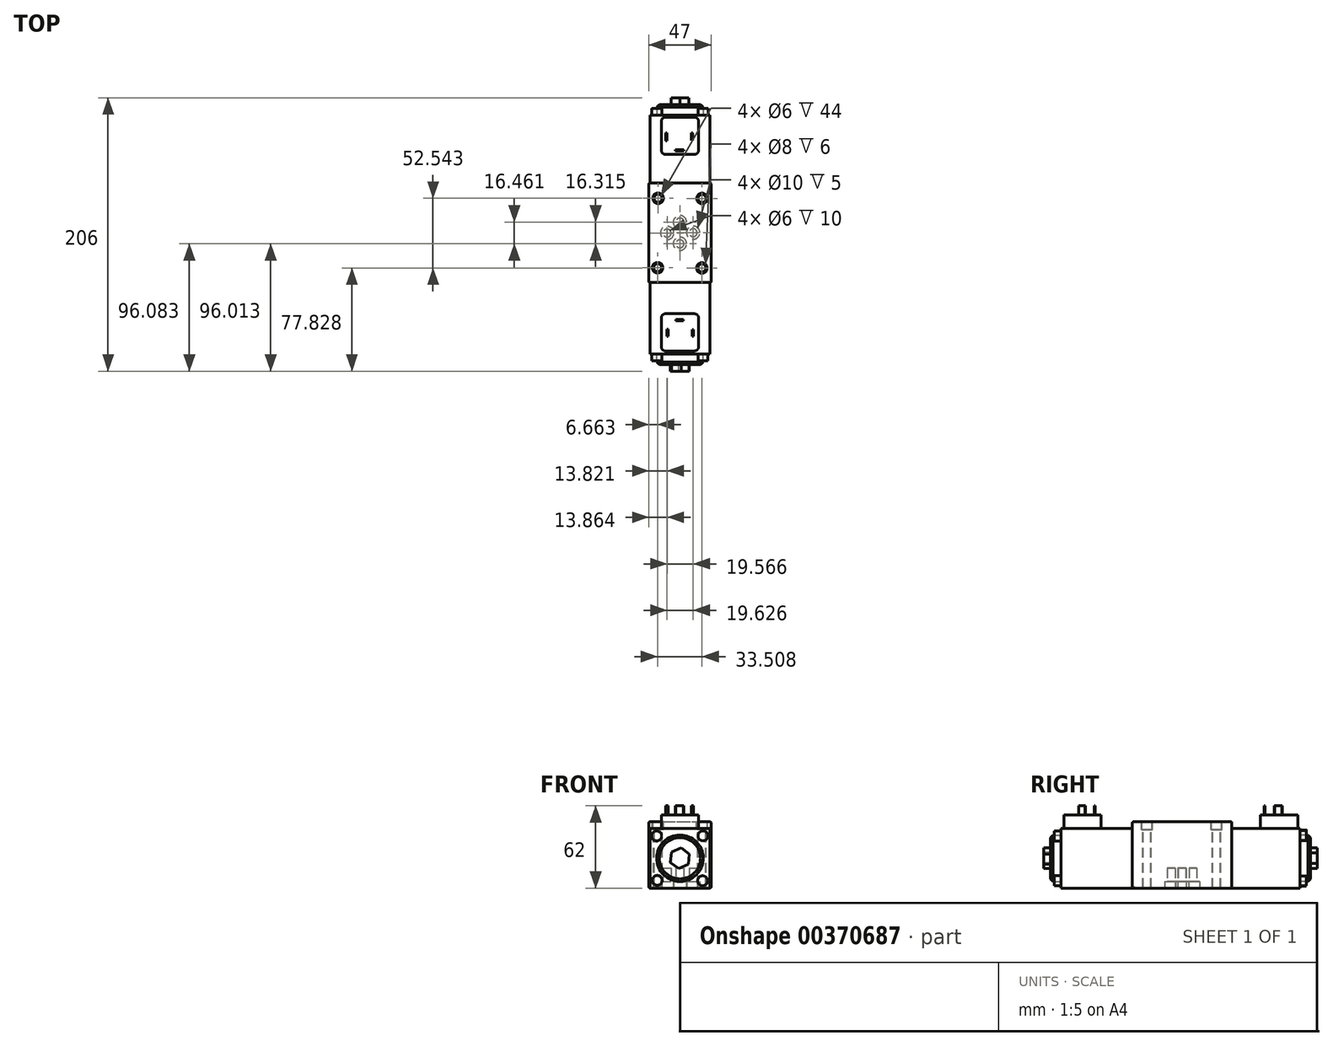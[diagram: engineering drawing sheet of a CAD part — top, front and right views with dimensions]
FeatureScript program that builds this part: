
annotation { "Feature Type Name" : "Feature", "Feature Type Description" : "" }
export const myFeature = defineFeature(function(context is Context, id is Id, definition is map)
    precondition{}
    {
        {
            var Q0;
            Q0=qCreatedBy(makeId("Front.planeOp"),FACE);
            var sketch = newSketch(context, id + "F0", { "sketchPlane" : qUnion([Q0])});
            skLineSegment(sketch, "E0.bottom", {"start": v(-22.5, 22.5) * mm, "end": v(22.5, 22.5) * mm});
            skLineSegment(sketch, "E0.top", {"start": v(-22.5, -22.5) * mm, "end": v(22.5, -22.5) * mm});
            skLineSegment(sketch, "E0.left", {"start": v(-22.5, 22.5) * mm, "end": v(-22.5, -22.5) * mm});
            skLineSegment(sketch, "E0.right", {"start": v(22.5, 22.5) * mm, "end": v(22.5, -22.5) * mm});
            skPoint(sketch, "E0.middle", {"position": v(0, 0) * mm});
            skSolve(sketch);
        }
        {
            var Q0;
            Q0=makeQuery(id+"F0.imprint","IMPRINT",FACE,{"disambiguationData":[TD([[makeQuery(id+"F0.imprint","IMPRINT",EDGE,{"derivedFrom":sQuery(id+"F0.wireOp",EDGE,"E0.bottom")}),-1.0]])]});
            extrude(context, id + "F1", {"entities" : qUnion([Q0]), "oppositeDirection" : true, "depth" : 180 * mm});
        }
        {
            var Q0;
            Q0=makeQuery(id+"F1.opExtrude","CAP_FACE",FACE,{"disambiguationData":[OSD([sQuery(id+"F0.wireOp",EDGE,"E0.bottom"),sQuery(id+"F0.wireOp",EDGE,"E0.top"),sQuery(id+"F0.wireOp",EDGE,"E0.left"),sQuery(id+"F0.wireOp",EDGE,"E0.right")])],"isStart":true});
            var sketch = newSketch(context, id + "F2", { "sketchPlane" : qUnion([Q0])});
            skCircle(sketch, "E1", {"center": v(0, 0) * mm, "radius": 17.5 * mm});
            skSolve(sketch);
        }
        {
            var Q0;
            Q0=makeQuery(id+"F2.imprint","IMPRINT",FACE,{"disambiguationData":[TD([[makeQuery(id+"F2.imprint","IMPRINT",EDGE,{"derivedFrom":sQuery(id+"F2.wireOp",EDGE,"E1")}),1.0]])]});
            extrude(context, id + "F3", {"entities" : qUnion([Q0]), "operationType" : NewBodyOperationType.ADD, "depth" : 8 * mm});
        }
        {
            var Q0;
            Q0=makeQuery(id+"F1.opExtrude","CAP_FACE",FACE,{"disambiguationData":[OSD([sQuery(id+"F0.wireOp",EDGE,"E0.bottom"),sQuery(id+"F0.wireOp",EDGE,"E0.top"),sQuery(id+"F0.wireOp",EDGE,"E0.left"),sQuery(id+"F0.wireOp",EDGE,"E0.right")])],"isStart":false});
            var sketch = newSketch(context, id + "F4", { "sketchPlane" : qUnion([Q0])});
            skCircle(sketch, "E2", {"center": v(0, 0) * mm, "radius": 17.5 * mm});
            skSolve(sketch);
        }
        {
            var Q0;
            Q0=makeQuery(id+"F4.imprint","IMPRINT",FACE,{"disambiguationData":[TD([[makeQuery(id+"F4.imprint","IMPRINT",EDGE,{"derivedFrom":sQuery(id+"F4.wireOp",EDGE,"E2")}),1.0]])]});
            extrude(context, id + "F5", {"entities" : qUnion([Q0]), "operationType" : NewBodyOperationType.ADD, "depth" : 8 * mm});
        }
        {
            var Q0;
            Q0=makeQuery(id+"F1.opExtrude","CAP_FACE",FACE,{"disambiguationData":[OSD([sQuery(id+"F0.wireOp",EDGE,"E0.bottom"),sQuery(id+"F0.wireOp",EDGE,"E0.top"),sQuery(id+"F0.wireOp",EDGE,"E0.left"),sQuery(id+"F0.wireOp",EDGE,"E0.right")])],"isStart":false});
            var sketch = newSketch(context, id + "F6", { "sketchPlane" : qUnion([Q0])});
            skSolve(sketch);
        }
        {
            var Q0;
            Q0=makeQuery(id+"F1.opExtrude","CAP_FACE",FACE,{"disambiguationData":[OSD([sQuery(id+"F0.wireOp",EDGE,"E0.bottom"),sQuery(id+"F0.wireOp",EDGE,"E0.top"),sQuery(id+"F0.wireOp",EDGE,"E0.left"),sQuery(id+"F0.wireOp",EDGE,"E0.right")])],"isStart":true});
            var sketch = newSketch(context, id + "F7", { "sketchPlane" : qUnion([Q0])});
            skCircle(sketch, "E3", {"center": v(17.33, 16.83) * mm, "radius": 3.75 * mm});
            skCircle(sketch, "E4", {"center": v(-17.5, 16.75) * mm, "radius": 3.75 * mm});
            skCircle(sketch, "E5", {"center": v(-17.1, -16.62) * mm, "radius": 3.75 * mm});
            skCircle(sketch, "E6", {"center": v(17.1, -16.96) * mm, "radius": 3.75 * mm});
            skSolve(sketch);
        }
        {
            var Q0;
            Q0=makeQuery(id+"F7.imprint","IMPRINT",FACE,{"disambiguationData":[TD([[makeQuery(id+"F7.imprint","IMPRINT",EDGE,{"derivedFrom":sQuery(id+"F7.wireOp",EDGE,"E6")}),1.0]])]});
            var Q1;
            Q1=makeQuery(id+"F7.imprint","IMPRINT",FACE,{"disambiguationData":[TD([[makeQuery(id+"F7.imprint","IMPRINT",EDGE,{"derivedFrom":sQuery(id+"F7.wireOp",EDGE,"E5")}),1.0]])]});
            var Q2;
            Q2=makeQuery(id+"F7.imprint","IMPRINT",FACE,{"disambiguationData":[TD([[makeQuery(id+"F7.imprint","IMPRINT",EDGE,{"derivedFrom":sQuery(id+"F7.wireOp",EDGE,"E3")}),1.0]])]});
            var Q3;
            Q3=makeQuery(id+"F7.imprint","IMPRINT",FACE,{"disambiguationData":[TD([[makeQuery(id+"F7.imprint","IMPRINT",EDGE,{"derivedFrom":sQuery(id+"F7.wireOp",EDGE,"E4")}),1.0]])]});
            extrude(context, id + "F8", {"entities" : qUnion([Q0, Q1, Q2, Q3]), "operationType" : NewBodyOperationType.ADD, "depth" : 5 * mm});
        }
        {
            var Q0;
            Q0=makeQuery(id+"F3.opExtrude","CAP_FACE",FACE,{"disambiguationData":[OSD([sQuery(id+"F2.wireOp",EDGE,"E1")])],"isStart":false});
            var sketch = newSketch(context, id + "F9", { "sketchPlane" : qUnion([Q0])});
            skCircle(sketch, "E7.cCircle", {"center": v(0, 0) * mm, "radius": 6.75 * mm, "construction": true});
            skLineSegment(sketch, "E7.0", {"start": v(-6.28, 4.61) * mm, "end": v(0.85, 7.75) * mm});
            skLineSegment(sketch, "E7.1", {"start": v(0.85, 7.75) * mm, "end": v(7.14, 3.13) * mm});
            skLineSegment(sketch, "E7.2", {"start": v(7.14, 3.13) * mm, "end": v(6.28, -4.61) * mm});
            skLineSegment(sketch, "E7.3", {"start": v(6.28, -4.61) * mm, "end": v(-0.85, -7.75) * mm});
            skLineSegment(sketch, "E7.4", {"start": v(-0.85, -7.75) * mm, "end": v(-7.14, -3.13) * mm});
            skLineSegment(sketch, "E7.5", {"start": v(-7.14, -3.13) * mm, "end": v(-6.28, 4.61) * mm});
            skPoint(sketch, "E7.0.midPoint", {"position": v(-2.71, 6.18) * mm});
            skSolve(sketch);
        }
        {
            var Q0;
            Q0 = qSketchRegion(id + "F9", true);
            extrude(context, id + "F10", {"entities" : qUnion([Q0]), "operationType" : NewBodyOperationType.ADD, "depth" : 5 * mm});
        }
        {
            var Q0;
            Q0=makeQuery(id+"F5.opExtrude","CAP_FACE",FACE,{"disambiguationData":[OSD([sQuery(id+"F4.wireOp",EDGE,"E2")])],"isStart":false});
            var sketch = newSketch(context, id + "F11", { "sketchPlane" : qUnion([Q0])});
            skCircle(sketch, "E8.cCircle", {"center": v(0, 0) * mm, "radius": 6.75 * mm, "construction": true});
            skLineSegment(sketch, "E8.0", {"start": v(-6.75, -3.9) * mm, "end": v(-6.75, 3.9) * mm});
            skLineSegment(sketch, "E8.1", {"start": v(-6.75, 3.9) * mm, "end": v(0, 7.8) * mm});
            skLineSegment(sketch, "E8.2", {"start": v(0, 7.8) * mm, "end": v(6.75, 3.9) * mm});
            skLineSegment(sketch, "E8.3", {"start": v(6.75, 3.9) * mm, "end": v(6.75, -3.9) * mm});
            skLineSegment(sketch, "E8.4", {"start": v(6.75, -3.9) * mm, "end": v(0, -7.8) * mm});
            skLineSegment(sketch, "E8.5", {"start": v(0, -7.8) * mm, "end": v(-6.75, -3.9) * mm});
            skPoint(sketch, "E8.0.midPoint", {"position": v(-6.75, 0) * mm});
            skSolve(sketch);
        }
        {
            var Q0;
            Q0 = qSketchRegion(id + "F11", true);
            extrude(context, id + "F12", {"entities" : qUnion([Q0]), "operationType" : NewBodyOperationType.ADD, "depth" : 5 * mm});
        }
        {
            var Q0;
            Q0=makeQuery(id+"F6.imprint","IMPRINT",FACE,{"disambiguationData":[TD([[makeQuery(id+"F6.imprint","IMPRINT",EDGE,{"derivedFrom":makeQuery(id+"F1.opExtrude","CAP_EDGE",EDGE,{"disambiguationData":[OSD([sQuery(id+"F0.wireOp",EDGE,"E0.bottom")])],"isStart":false})}),1.0]])]});
            var sketch = newSketch(context, id + "F13", { "sketchPlane" : qUnion([Q0])});
            skCircle(sketch, "E9", {"center": v(-17.56, 17.13) * mm, "radius": 3.75 * mm});
            skCircle(sketch, "E10", {"center": v(17.36, 17.52) * mm, "radius": 3.75 * mm});
            skCircle(sketch, "E11", {"center": v(-17.32, -17.12) * mm, "radius": 3.75 * mm});
            skCircle(sketch, "E12", {"center": v(17.37, -17.42) * mm, "radius": 3.75 * mm});
            skSolve(sketch);
        }
        {
            var Q0;
            Q0 = qSketchRegion(id + "F13", true);
            extrude(context, id + "F14", {"entities" : qUnion([Q0]), "operationType" : NewBodyOperationType.ADD, "depth" : 5 * mm});
        }
        {
            var Q0;
            Q0=makeQuery(id+"F3.opExtrude","CAP_EDGE",EDGE,{"disambiguationData":[OSD([sQuery(id+"F2.wireOp",EDGE,"E1")])],"isStart":false});
            chamfer(context, id + "F15", {"entities" : qUnion([Q0]), "width" : 2 * mm, "tangentPropagation" : true});
        }
        {
            var Q0;
            Q0=makeQuery(id+"F5.opExtrude","CAP_EDGE",EDGE,{"disambiguationData":[OSD([sQuery(id+"F4.wireOp",EDGE,"E2")])],"isStart":false});
            chamfer(context, id + "F16", {"entities" : qUnion([Q0]), "width" : 2 * mm, "tangentPropagation" : true});
        }
        {
            var Q0;
            Q0=makeQuery(id+"F1.opExtrude","SWEPT_FACE",FACE,{"disambiguationData":[OSD([sQuery(id+"F0.wireOp",EDGE,"E0.bottom")])]});
            var sketch = newSketch(context, id + "F17", { "sketchPlane" : qUnion([Q0])});
            skLineSegment(sketch, "E13.bottom", {"start": v(-11, 30.3) * mm, "end": v(11, 30.3) * mm});
            skLineSegment(sketch, "E13.top", {"start": v(-11, 2.3) * mm, "end": v(11, 2.3) * mm});
            skLineSegment(sketch, "E13.left", {"start": v(-14, 27.3) * mm, "end": v(-14, 5.3) * mm});
            skLineSegment(sketch, "E13.right", {"start": v(14, 27.3) * mm, "end": v(14, 5.3) * mm});
            skPoint(sketch, "E13.middle", {"position": v(0, 16.3) * mm});
            skLineSegment(sketch, "E14.bottom", {"start": v(11, 150.42) * mm, "end": v(-11, 150.42) * mm});
            skLineSegment(sketch, "E14.top", {"start": v(11, 178.42) * mm, "end": v(-11, 178.42) * mm});
            skLineSegment(sketch, "E14.left", {"start": v(14, 153.42) * mm, "end": v(14, 175.42) * mm});
            skLineSegment(sketch, "E14.right", {"start": v(-14, 153.42) * mm, "end": v(-14, 175.42) * mm});
            skPoint(sketch, "E14.middle", {"position": v(0, 164.42) * mm});
            skPoint(sketch, "E15.visualSharp", {"position": v(14, 178.42) * mm});
            skArc(sketch, "E15.filletArc", {"start": v(14, 175.42) * mm, "mid": v(13.12, 177.54) * mm, "end": v(11, 178.42) * mm});
            skPoint(sketch, "E16.visualSharp", {"position": v(14, 150.42) * mm});
            skArc(sketch, "E16.filletArc", {"start": v(11, 150.42) * mm, "mid": v(13.12, 151.3) * mm, "end": v(14, 153.42) * mm});
            skPoint(sketch, "E17.visualSharp", {"position": v(-14, 150.42) * mm});
            skArc(sketch, "E17.filletArc", {"start": v(-14, 153.42) * mm, "mid": v(-13.12, 151.3) * mm, "end": v(-11, 150.42) * mm});
            skPoint(sketch, "E18.visualSharp", {"position": v(-14, 178.42) * mm});
            skArc(sketch, "E18.filletArc", {"start": v(-11, 178.42) * mm, "mid": v(-13.12, 177.54) * mm, "end": v(-14, 175.42) * mm});
            skPoint(sketch, "E19.visualSharp", {"position": v(14, 30.3) * mm});
            skArc(sketch, "E19.filletArc", {"start": v(14, 27.3) * mm, "mid": v(13.12, 29.43) * mm, "end": v(11, 30.3) * mm});
            skPoint(sketch, "E20.visualSharp", {"position": v(14, 2.3) * mm});
            skArc(sketch, "E20.filletArc", {"start": v(11, 2.3) * mm, "mid": v(13.12, 3.19) * mm, "end": v(14, 5.3) * mm});
            skPoint(sketch, "E21.visualSharp", {"position": v(-14, 2.3) * mm});
            skArc(sketch, "E21.filletArc", {"start": v(-14, 5.3) * mm, "mid": v(-13.12, 3.19) * mm, "end": v(-11, 2.3) * mm});
            skPoint(sketch, "E22.visualSharp", {"position": v(-14, 30.3) * mm});
            skArc(sketch, "E22.filletArc", {"start": v(-11, 30.3) * mm, "mid": v(-13.12, 29.43) * mm, "end": v(-14, 27.3) * mm});
            skSolve(sketch);
        }
        {
            var Q0;
            Q0=makeQuery(id+"F17.imprint","IMPRINT",FACE,{"disambiguationData":[TD([[makeQuery(id+"F17.imprint","IMPRINT",EDGE,{"derivedFrom":sQuery(id+"F17.wireOp",EDGE,"E14.bottom")}),-1.0]])]});
            var Q1;
            Q1=makeQuery(id+"F17.imprint","IMPRINT",FACE,{"disambiguationData":[TD([[makeQuery(id+"F17.imprint","IMPRINT",EDGE,{"derivedFrom":sQuery(id+"F17.wireOp",EDGE,"E13.bottom")}),-1.0]])]});
            extrude(context, id + "F18", {"entities" : qUnion([Q0, Q1]), "operationType" : NewBodyOperationType.ADD, "depth" : 10 * mm});
        }
        {
            var Q0;
            Q0=makeQuery(id+"F1.opExtrude","SWEPT_FACE",FACE,{"disambiguationData":[OSD([sQuery(id+"F0.wireOp",EDGE,"E0.bottom")])]});
            var sketch = newSketch(context, id + "F19", { "sketchPlane" : qUnion([Q0])});
            skLineSegment(sketch, "E23.bottom", {"start": v(-23.5, 128.83) * mm, "end": v(23.5, 128.83) * mm});
            skLineSegment(sketch, "E23.top", {"start": v(-23.5, 53.83) * mm, "end": v(23.5, 53.83) * mm});
            skLineSegment(sketch, "E23.left", {"start": v(-23.5, 128.83) * mm, "end": v(-23.5, 53.83) * mm});
            skLineSegment(sketch, "E23.right", {"start": v(23.5, 128.83) * mm, "end": v(23.5, 53.83) * mm});
            skPoint(sketch, "E23.middle", {"position": v(0, 91.33) * mm});
            skSolve(sketch);
        }
        {
            var Q0;
            Q0 = qSketchRegion(id + "F19", true);
            extrude(context, id + "F20", {"entities" : qUnion([Q0]), "operationType" : NewBodyOperationType.ADD, "depth" : 5 * mm});
        }
        {
            var Q0;
            Q0=makeQuery(id+"F1.opExtrude","SWEPT_FACE",FACE,{"disambiguationData":[OSD([sQuery(id+"F0.wireOp",EDGE,"E0.right")])]});
            var sketch = newSketch(context, id + "F21", { "sketchPlane" : qUnion([Q0])});
            skLineSegment(sketch, "E24.bottom", {"start": v(53.83, 22.5) * mm, "end": v(128.83, 22.5) * mm});
            skLineSegment(sketch, "E24.top", {"start": v(53.83, -22.5) * mm, "end": v(128.83, -22.5) * mm});
            skLineSegment(sketch, "E24.left", {"start": v(53.83, 22.5) * mm, "end": v(53.83, -22.5) * mm});
            skLineSegment(sketch, "E24.right", {"start": v(128.83, 22.5) * mm, "end": v(128.83, -22.5) * mm});
            skPoint(sketch, "E24.middle", {"position": v(91.33, 0) * mm});
            skSolve(sketch);
        }
        {
            var Q0;
            Q0=makeQuery(id+"F21.imprint","IMPRINT",FACE,{"disambiguationData":[TD([[makeQuery(id+"F21.imprint","IMPRINT",EDGE,{"derivedFrom":sQuery(id+"F21.wireOp",EDGE,"E24.bottom")}),1.0]])]});
            extrude(context, id + "F22", {"entities" : qUnion([Q0]), "operationType" : NewBodyOperationType.ADD, "depth" : 1 * mm});
        }
        {
            var Q0;
            Q0=makeQuery(id+"F1.opExtrude","SWEPT_FACE",FACE,{"disambiguationData":[OSD([sQuery(id+"F0.wireOp",EDGE,"E0.left")])]});
            var sketch = newSketch(context, id + "F23", { "sketchPlane" : qUnion([Q0])});
            skLineSegment(sketch, "E25.bottom", {"start": v(-128.83, 22.5) * mm, "end": v(-53.83, 22.5) * mm});
            skLineSegment(sketch, "E25.top", {"start": v(-128.83, -22.5) * mm, "end": v(-53.83, -22.5) * mm});
            skLineSegment(sketch, "E25.left", {"start": v(-128.83, 22.5) * mm, "end": v(-128.83, -22.5) * mm});
            skLineSegment(sketch, "E25.right", {"start": v(-53.83, 22.5) * mm, "end": v(-53.83, -22.5) * mm});
            skPoint(sketch, "E25.middle", {"position": v(-91.33, 0) * mm});
            skSolve(sketch);
        }
        {
            var Q0;
            Q0=makeQuery(id+"F23.imprint","IMPRINT",FACE,{"disambiguationData":[TD([[makeQuery(id+"F23.imprint","IMPRINT",EDGE,{"derivedFrom":sQuery(id+"F23.wireOp",EDGE,"E25.bottom")}),-1.0]])]});
            extrude(context, id + "F24", {"entities" : qUnion([Q0]), "operationType" : NewBodyOperationType.ADD, "depth" : 1 * mm});
        }
        {
            var Q0;
            Q0=makeQuery(id+"F24.boolean.opBoolean","MERGE",FACE,{"derivedFrom":[makeQuery(id+"F22.boolean.opBoolean","MERGE",FACE,{"derivedFrom":[makeQuery(id+"F1.opExtrude","SWEPT_FACE",FACE,{"disambiguationData":[OSD([sQuery(id+"F0.wireOp",EDGE,"E0.top")])]}),makeQuery(id+"F22.opExtrude","SWEPT_FACE",FACE,{"disambiguationData":[OSD([sQuery(id+"F21.wireOp",EDGE,"E24.top")])]})]}),makeQuery(id+"F24.opExtrude","SWEPT_FACE",FACE,{"disambiguationData":[OSD([sQuery(id+"F23.wireOp",EDGE,"E25.top")])]})]});
            var sketch = newSketch(context, id + "F25", { "sketchPlane" : qUnion([Q0])});
            skLineSegment(sketch, "E26.bottom", {"start": v(-23.5, -53.83) * mm, "end": v(23.5, -53.83) * mm});
            skLineSegment(sketch, "E26.top", {"start": v(-23.5, -128.83) * mm, "end": v(23.5, -128.83) * mm});
            skLineSegment(sketch, "E26.left", {"start": v(-23.5, -53.83) * mm, "end": v(-23.5, -128.83) * mm});
            skLineSegment(sketch, "E26.right", {"start": v(23.5, -53.83) * mm, "end": v(23.5, -128.83) * mm});
            skPoint(sketch, "E26.middle", {"position": v(0, -91.33) * mm});
            skSolve(sketch);
        }
        {
            var Q0;
            Q0=makeQuery(id+"F20.opExtrude","CAP_FACE",FACE,{"disambiguationData":[OSD([sQuery(id+"F19.wireOp",EDGE,"E23.bottom"),sQuery(id+"F19.wireOp",EDGE,"E23.top"),sQuery(id+"F19.wireOp",EDGE,"E23.left"),sQuery(id+"F19.wireOp",EDGE,"E23.right")])],"isStart":false});
            fillet(context, id + "F26", {"entities" : qUnion([Q0]), "radius" : 1 * mm, "tangentPropagation" : true, "allowEdgeOverflow" : false});
        }
        {
            var Q0;
            Q0=makeQuery(id+"F24.boolean.opBoolean","MERGE",FACE,{"derivedFrom":[makeQuery(id+"F20.opExtrude","SWEPT_FACE",FACE,{"disambiguationData":[OSD([sQuery(id+"F19.wireOp",EDGE,"E23.left")])]}),makeQuery(id+"F24.opExtrude","CAP_FACE",FACE,{"disambiguationData":[OSD([sQuery(id+"F23.wireOp",EDGE,"E25.bottom"),sQuery(id+"F23.wireOp",EDGE,"E25.top"),sQuery(id+"F23.wireOp",EDGE,"E25.left"),sQuery(id+"F23.wireOp",EDGE,"E25.right")])],"isStart":false})]});
            fillet(context, id + "F27", {"entities" : qUnion([Q0]), "radius" : 1 * mm, "tangentPropagation" : true, "allowEdgeOverflow" : false});
        }
        {
            var Q0;
            Q0=makeQuery(id+"F22.boolean.opBoolean","MERGE",FACE,{"derivedFrom":[makeQuery(id+"F20.opExtrude","SWEPT_FACE",FACE,{"disambiguationData":[OSD([sQuery(id+"F19.wireOp",EDGE,"E23.right")])]}),makeQuery(id+"F22.opExtrude","CAP_FACE",FACE,{"disambiguationData":[OSD([sQuery(id+"F21.wireOp",EDGE,"E24.bottom"),sQuery(id+"F21.wireOp",EDGE,"E24.top"),sQuery(id+"F21.wireOp",EDGE,"E24.left"),sQuery(id+"F21.wireOp",EDGE,"E24.right")])],"isStart":false})]});
            fillet(context, id + "F28", {"entities" : qUnion([Q0]), "radius" : 1 * mm, "tangentPropagation" : true, "allowEdgeOverflow" : false});
        }
        {
            var Q0;
            Q0=makeQuery(id+"F18.opExtrude","CAP_FACE",FACE,{"disambiguationData":[OSD([sQuery(id+"F17.wireOp",EDGE,"E14.bottom"),sQuery(id+"F17.wireOp",EDGE,"E14.top"),sQuery(id+"F17.wireOp",EDGE,"E14.left"),sQuery(id+"F17.wireOp",EDGE,"E14.right"),sQuery(id+"F17.wireOp",EDGE,"E15.filletArc"),sQuery(id+"F17.wireOp",EDGE,"E16.filletArc"),sQuery(id+"F17.wireOp",EDGE,"E17.filletArc"),sQuery(id+"F17.wireOp",EDGE,"E18.filletArc")])],"isStart":false});
            var sketch = newSketch(context, id + "F29", { "sketchPlane" : qUnion([Q0])});
            skSolve(sketch);
        }
        {
            var Q0;
            Q0=makeQuery(id+"F18.opExtrude","CAP_FACE",FACE,{"disambiguationData":[OSD([sQuery(id+"F17.wireOp",EDGE,"E13.bottom"),sQuery(id+"F17.wireOp",EDGE,"E13.top"),sQuery(id+"F17.wireOp",EDGE,"E13.left"),sQuery(id+"F17.wireOp",EDGE,"E13.right"),sQuery(id+"F17.wireOp",EDGE,"E19.filletArc"),sQuery(id+"F17.wireOp",EDGE,"E20.filletArc"),sQuery(id+"F17.wireOp",EDGE,"E21.filletArc"),sQuery(id+"F17.wireOp",EDGE,"E22.filletArc")])],"isStart":false});
            var sketch = newSketch(context, id + "F30", { "sketchPlane" : qUnion([Q0])});
            skLineSegment(sketch, "E27.bottom", {"start": v(-3.21, 25.89) * mm, "end": v(2.6, 25.89) * mm});
            skLineSegment(sketch, "E27.top", {"start": v(-3.21, 25.14) * mm, "end": v(2.6, 25.14) * mm});
            skLineSegment(sketch, "E27.left", {"start": v(-3.21, 25.89) * mm, "end": v(-3.21, 25.14) * mm});
            skLineSegment(sketch, "E27.right", {"start": v(2.6, 25.89) * mm, "end": v(2.6, 25.14) * mm});
            skLineSegment(sketch, "E28.bottom", {"start": v(9.28, 18.34) * mm, "end": v(10.13, 18.34) * mm});
            skLineSegment(sketch, "E28.top", {"start": v(9.28, 13.42) * mm, "end": v(10.13, 13.42) * mm});
            skLineSegment(sketch, "E28.left", {"start": v(9.28, 18.34) * mm, "end": v(9.28, 13.42) * mm});
            skLineSegment(sketch, "E28.right", {"start": v(10.13, 18.34) * mm, "end": v(10.13, 13.42) * mm});
            skLineSegment(sketch, "E29.bottom", {"start": v(-9.85, 18.57) * mm, "end": v(-8.97, 18.57) * mm});
            skLineSegment(sketch, "E29.top", {"start": v(-9.85, 13.42) * mm, "end": v(-8.97, 13.42) * mm});
            skLineSegment(sketch, "E29.left", {"start": v(-9.85, 18.57) * mm, "end": v(-9.85, 13.42) * mm});
            skLineSegment(sketch, "E29.right", {"start": v(-8.97, 18.57) * mm, "end": v(-8.97, 13.42) * mm});
            skSolve(sketch);
        }
        {
            var Q0;
            Q0 = qSketchRegion(id + "F30", true);
            extrude(context, id + "F31", {"entities" : qUnion([Q0]), "operationType" : NewBodyOperationType.ADD, "depth" : 7 * mm});
        }
        {
            var Q0;
            Q0=makeQuery(id+"F29.imprint","IMPRINT",FACE,{"disambiguationData":[TD([[makeQuery(id+"F29.imprint","IMPRINT",EDGE,{"derivedFrom":makeQuery(id+"F18.opExtrude","CAP_EDGE",EDGE,{"disambiguationData":[OSD([sQuery(id+"F17.wireOp",EDGE,"E14.bottom")])],"isStart":false})}),-1.0]])]});
            var sketch = newSketch(context, id + "F32", { "sketchPlane" : qUnion([Q0])});
            skLineSegment(sketch, "E30.bottom", {"start": v(-3.34, 153.83) * mm, "end": v(2.8, 153.83) * mm});
            skLineSegment(sketch, "E30.top", {"start": v(-3.34, 153.12) * mm, "end": v(2.8, 153.12) * mm});
            skLineSegment(sketch, "E30.left", {"start": v(-3.34, 153.83) * mm, "end": v(-3.34, 153.12) * mm});
            skLineSegment(sketch, "E30.right", {"start": v(2.8, 153.83) * mm, "end": v(2.8, 153.12) * mm});
            skLineSegment(sketch, "E31.bottom", {"start": v(-10.88, 166.8) * mm, "end": v(-9.94, 166.8) * mm});
            skLineSegment(sketch, "E31.top", {"start": v(-10.88, 160.67) * mm, "end": v(-9.94, 160.67) * mm});
            skLineSegment(sketch, "E31.left", {"start": v(-10.88, 166.8) * mm, "end": v(-10.88, 160.67) * mm});
            skLineSegment(sketch, "E31.right", {"start": v(-9.94, 166.8) * mm, "end": v(-9.94, 160.67) * mm});
            skLineSegment(sketch, "E32.bottom", {"start": v(8.69, 166.56) * mm, "end": v(9.63, 166.56) * mm});
            skLineSegment(sketch, "E32.top", {"start": v(8.69, 160.9) * mm, "end": v(9.63, 160.9) * mm});
            skLineSegment(sketch, "E32.left", {"start": v(8.69, 166.56) * mm, "end": v(8.69, 160.9) * mm});
            skLineSegment(sketch, "E32.right", {"start": v(9.63, 166.56) * mm, "end": v(9.63, 160.9) * mm});
            skSolve(sketch);
        }
        {
            var Q0;
            Q0 = qSketchRegion(id + "F32", true);
            extrude(context, id + "F33", {"entities" : qUnion([Q0]), "operationType" : NewBodyOperationType.ADD, "depth" : 7 * mm});
        }
        {
            var Q0;
            Q0=makeQuery(id+"F20.opExtrude","CAP_FACE",FACE,{"disambiguationData":[OSD([sQuery(id+"F19.wireOp",EDGE,"E23.bottom"),sQuery(id+"F19.wireOp",EDGE,"E23.top"),sQuery(id+"F19.wireOp",EDGE,"E23.left"),sQuery(id+"F19.wireOp",EDGE,"E23.right")])],"isStart":false});
            var sketch = newSketch(context, id + "F34", { "sketchPlane" : qUnion([Q0])});
            skCircle(sketch, "E33", {"center": v(-16.43, 117.37) * mm, "radius": 3 * mm});
            skCircle(sketch, "E34", {"center": v(16.67, 117.2) * mm, "radius": 3 * mm});
            skCircle(sketch, "E35", {"center": v(-16.84, 65.02) * mm, "radius": 3 * mm});
            skCircle(sketch, "E36", {"center": v(16.52, 64.83) * mm, "radius": 3 * mm});
            skSolve(sketch);
        }
        {
            var Q0;
            Q0 = qSketchRegion(id + "F34", true);
            extrude(context, id + "F35", {"entities" : qUnion([Q0]), "operationType" : NewBodyOperationType.REMOVE, "endBound" : BoundingType.THROUGH_ALL, "oppositeDirection" : true, "depth" : 50 * mm});
        }
        {
            var Q0;
            Q0=makeQuery(id+"F20.opExtrude","CAP_FACE",FACE,{"disambiguationData":[OSD([sQuery(id+"F19.wireOp",EDGE,"E23.bottom"),sQuery(id+"F19.wireOp",EDGE,"E23.top"),sQuery(id+"F19.wireOp",EDGE,"E23.left"),sQuery(id+"F19.wireOp",EDGE,"E23.right")])],"isStart":false});
            var sketch = newSketch(context, id + "F36", { "sketchPlane" : qUnion([Q0])});
            skCircle(sketch, "E37", {"center": v(-16.43, 117.37) * mm, "radius": 4 * mm});
            skCircle(sketch, "E38", {"center": v(16.67, 117.2) * mm, "radius": 4 * mm});
            skCircle(sketch, "E39", {"center": v(-16.84, 65.02) * mm, "radius": 4 * mm});
            skCircle(sketch, "E40", {"center": v(16.52, 64.83) * mm, "radius": 4 * mm});
            skSolve(sketch);
        }
        {
            var Q0;
            Q0 = qSketchRegion(id + "F36", true);
            extrude(context, id + "F37", {"entities" : qUnion([Q0]), "operationType" : NewBodyOperationType.REMOVE, "oppositeDirection" : true, "depth" : 6 * mm});
        }
        {
            var Q0;
            {var subQ23=sQuery(id+"F25.wireOp",EDGE,"E26.left");Q0=makeQuery(id+"F25.imprint","IMPRINT",FACE,{"disambiguationData":[TD([[makeQuery(id+"F25.imprint","IMPRINT",EDGE,{"derivedFrom":subQ23}),-1.0]])]});}
            var sketch = newSketch(context, id + "F38", { "sketchPlane" : qUnion([Q0])});
            skCircle(sketch, "E41", {"center": v(9.95, -91.34) * mm, "radius": 3 * mm});
            skCircle(sketch, "E42", {"center": v(0, -83.01) * mm, "radius": 3 * mm});
            skCircle(sketch, "E43", {"center": v(-9.68, -91.06) * mm, "radius": 3 * mm});
            skCircle(sketch, "E44", {"center": v(0, -99.47) * mm, "radius": 3 * mm});
            skSolve(sketch);
        }
        {
            var Q0;
            Q0 = qSketchRegion(id + "F38", true);
            extrude(context, id + "F39", {"entities" : qUnion([Q0]), "operationType" : NewBodyOperationType.REMOVE, "oppositeDirection" : true, "depth" : 15 * mm});
        }
        {
            var Q0;
            {var subQ23=sQuery(id+"F25.wireOp",EDGE,"E26.left");Q0=makeQuery(id+"F25.imprint","IMPRINT",FACE,{"disambiguationData":[TD([[makeQuery(id+"F25.imprint","IMPRINT",EDGE,{"derivedFrom":subQ23}),-1.0]])]});}
            var sketch = newSketch(context, id + "F40", { "sketchPlane" : qUnion([Q0])});
            skCircle(sketch, "E45", {"center": v(-9.64, -91.2) * mm, "radius": 5 * mm});
            skCircle(sketch, "E46", {"center": v(0, -83.08) * mm, "radius": 5 * mm});
            skCircle(sketch, "E47", {"center": v(9.93, -91.4) * mm, "radius": 5 * mm});
            skCircle(sketch, "E48", {"center": v(0, -99.4) * mm, "radius": 5 * mm});
            skSolve(sketch);
        }
        {
            var Q0;
            Q0 = qSketchRegion(id + "F40", true);
            extrude(context, id + "F41", {"entities" : qUnion([Q0]), "operationType" : NewBodyOperationType.REMOVE, "oppositeDirection" : true, "depth" : 5 * mm});
        }
    });
